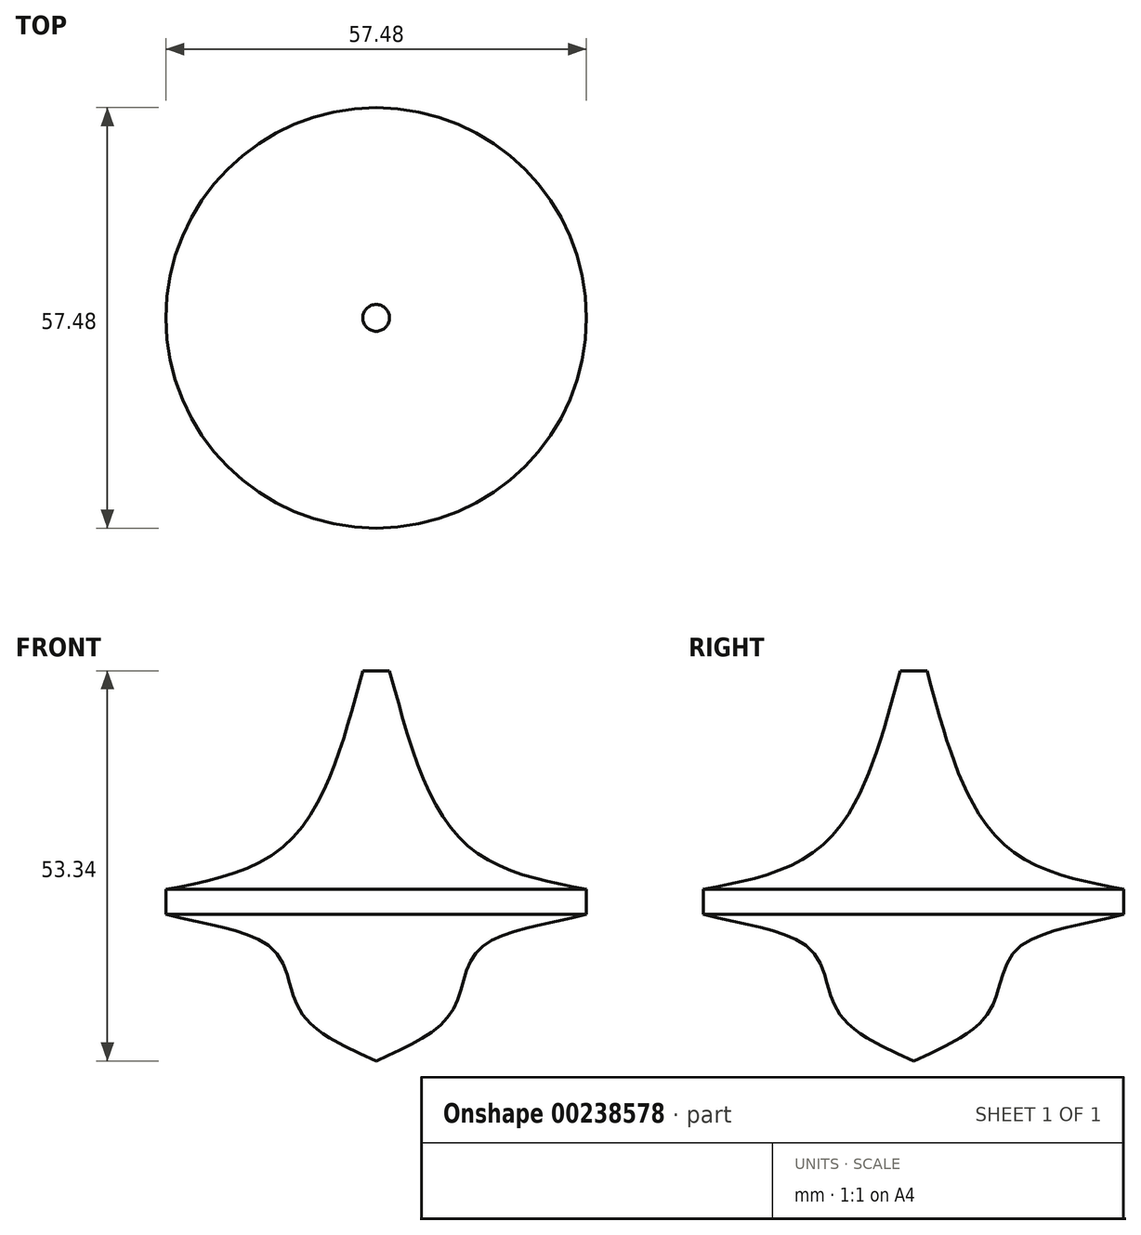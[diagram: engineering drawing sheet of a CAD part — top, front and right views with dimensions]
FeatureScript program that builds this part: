
annotation { "Feature Type Name" : "Feature", "Feature Type Description" : "" }
export const myFeature = defineFeature(function(context is Context, id is Id, definition is map)
    precondition{}
    {
        {
            var Q0;
            Q0=qCreatedBy(makeId("Front.planeOp"),FACE);
            var sketch = newSketch(context, id + "F0", { "sketchPlane" : qUnion([Q0])});
            skFitSpline(sketch, "E0", {"points": [v(0, 0) * mm, v(10.33, 6.74) * mm, v(13.87, 15.04) * mm, v(28.74, 20.06) * mm], "startDerivative": vector(37.63, 17.21) * mm, "endDerivative": vector(47.09, 13) * mm});
            skLineSegment(sketch, "E1", {"start": v(28.74, 20.06) * mm, "end": v(28.74, 23.45) * mm});
            skFitSpline(sketch, "E2", {"points": [v(28.74, 23.45) * mm, v(11.87, 30.01) * mm, v(1.83, 53.34) * mm], "startDerivative": vector(-40.67, 7.8) * mm, "endDerivative": vector(-13.91, 51.26) * mm});
            skLineSegment(sketch, "E3", {"start": v(1.83, 53.34) * mm, "end": v(0, 53.34) * mm});
            skLineSegment(sketch, "E4", {"start": v(0, 53.34) * mm, "end": v(0, 0) * mm});
            skSolve(sketch);
        }
        {
            var Q0;
            Q0 = qSketchRegion(id + "F0", true);
            var Q1;
            Q1=sQuery(id+"F0.wireOp",EDGE,"E4");
            revolve(context, id + "F1", {"entities" : qUnion([Q0]), "axis" : qUnion([Q1]), "revolveType" : RevolveType.FULL});
        }
    });
